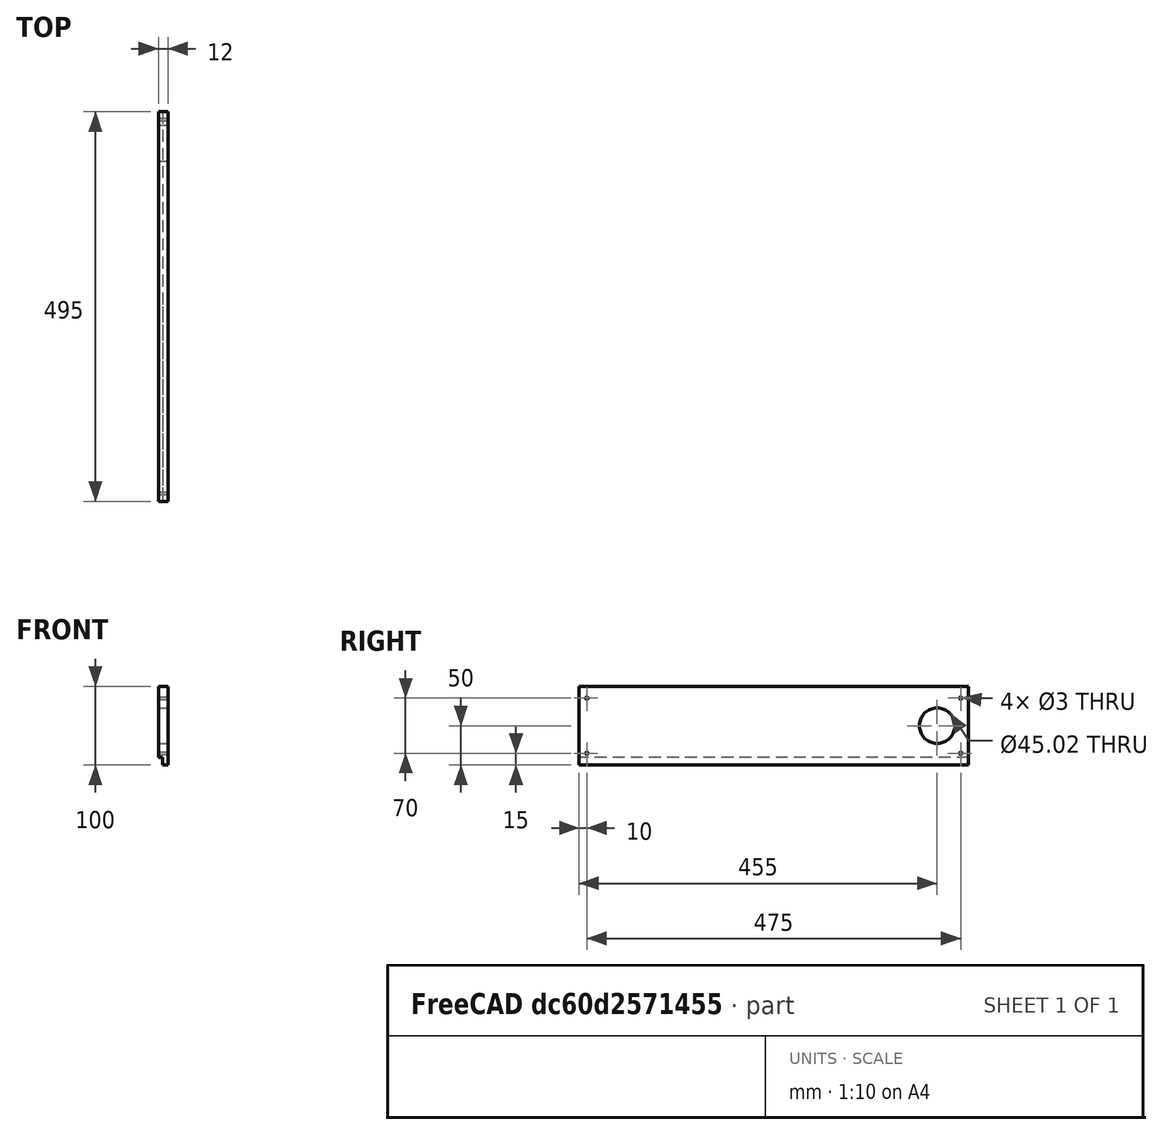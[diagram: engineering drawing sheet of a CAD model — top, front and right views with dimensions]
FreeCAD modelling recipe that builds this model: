
FCSTD DOCUMENT  (FreeCAD 0.20R29177 (Git))
Label: 8000_WindowFrameTopBack_
License: All rights reserved
LicenseURL: http://en.wikipedia.org/wiki/All_rights_reserved
objects: TechDraw::DrawViewDimension×8, Sketcher::SketchObject×3, PartDesign::Pocket×2, TechDraw::DrawViewPart×2, Spreadsheet::Sheet×1, PartDesign::Pad×1, TechDraw::DrawSVGTemplate×1, PartDesign::Body×1, TechDraw::DrawPage×1
note: 10 computed .brp shape members not serialized (recipe doc carries the construction recipe); baked Part::Feature solids carry a one-line shape summary decoded from their .brp

FEATURE [Sketcher::SketchObject] Sketch
  FullyConstrained = true
  MapMode = 4
  Placement = pos=(0,0,0) rot=(0.57735,0.57735,0.57735;2.0944rad)
  Support = -> [XY_Plane]
  expr: Constraints[5] = Spreadsheet.nZ
  expr: Constraints[6] = Spreadsheet.nY
  sketch-geometry (5):
    g0: LineSegment StartX=0 StartY=0 StartZ=0 EndX=0 EndY=100 EndZ=0
    g1: LineSegment StartX=495 StartY=0 StartZ=0 EndX=495 EndY=100 EndZ=0
    g2: LineSegment StartX=495 StartY=100 StartZ=0 EndX=0 EndY=100 EndZ=0
    g3: LineSegment StartX=247.5 StartY=0 StartZ=0 EndX=0 EndY=0 EndZ=0
    g4: LineSegment StartX=495 StartY=0 StartZ=0 EndX=247.5 EndY=0 EndZ=0
  constraints (14):
    c: Vertical(g0)
    c: Vertical(g1)
    c: Coincident(g2,g1)
    c: Coincident(g2,g0)
    c: Horizontal(g2)
    c: DistanceY(g1,g1) = 100
    c: DistanceX(g2,g2) = 495
    c: Coincident(g3,g0)
    c: Coincident(g4,g1)
    c: Horizontal(g4)
    c: Equal(g3,g4)
    c: Coincident(g4,g3)
    c: Horizontal(g3)
    c: Coincident(g0,g-1)
FEATURE [Spreadsheet::Sheet] Spreadsheet  label="xls"
  cells = B2=BODY FLOOR; E2=Ex.Ref.; B3=Thichness; C3=.T; D3=12; E3=mm; B7=KEYBOARD FRONT; D7=Sperrholz Birke 12 mm; B8=Width; C8=nY; D8(nY)=495; B9=Height; C9=nZ; D9(nZ)=100; E9=F(T); B10=Thickness; C10=nT; D10(nT)=12
FEATURE [PartDesign::Pad] Pad
  AllowMultiFace = false
  Direction = (1,1,1)
  Length = 12
  Length2 = 100
  Profile = -> Sketch
  Reversed = true
  Type = 0
  expr: Length = Spreadsheet.nT
FEATURE [Sketcher::SketchObject] Sketch001
  ExternalGeometry = -> [Pad]
  FullyConstrained = false
  MapMode = 5
  Placement = pos=(0,0,0) rot=(0.57735,0.57735,0.57735;2.0944rad)
  Support = -> [Pad]
  sketch-geometry (9):
    g0: LineSegment StartX=10 StartY=85 StartZ=0 EndX=485 EndY=85 EndZ=0
    g1: LineSegment StartX=485 StartY=85 StartZ=0 EndX=485 EndY=15 EndZ=0
    g2: LineSegment StartX=485 StartY=15 StartZ=0 EndX=10 EndY=15 EndZ=0
    g3: LineSegment StartX=10 StartY=15 StartZ=0 EndX=10 EndY=85 EndZ=0
    g4: Circle CenterX=10 CenterY=85 CenterZ=0 NormalX=0 NormalY=0 NormalZ=1 AngleXU=0 Radius=1.5
    g5: Circle CenterX=10 CenterY=15 CenterZ=0 NormalX=0 NormalY=0 NormalZ=1 AngleXU=0 Radius=1.5
    g6: Circle CenterX=485 CenterY=15 CenterZ=0 NormalX=0 NormalY=0 NormalZ=1 AngleXU=0 Radius=1.5
    g7: Circle CenterX=485 CenterY=85 CenterZ=0 NormalX=0 NormalY=0 NormalZ=1 AngleXU=0 Radius=1.5
    g8: Circle CenterX=455 CenterY=50 CenterZ=0 NormalX=0 NormalY=0 NormalZ=1 AngleXU=0 Radius=22.5086
  constraints (22):
    c: Coincident(g0,g1)
    c: Coincident(g1,g2)
    c: Coincident(g2,g3)
    c: Coincident(g3,g0)
    c: Horizontal(g0)
    c: Horizontal(g2)
    c: Vertical(g1)
    c: Vertical(g3)
    c: Coincident(g4,g0)
    c: Coincident(g5,g2)
    c: Coincident(g6,g1)
    c: Coincident(g7,g0)
    c: Equal(g4,g5)
    c: Equal(g5,g6)
    c: Equal(g6,g7)
    c: Diameter(g4) = 3
    c: DistanceY(g4,g-3) = 15
    c: DistanceX(g-3,g4) = 10
    c: DistanceY(g-1,g5) = 15
    c: DistanceX(g7,g-3) = 10
    c: DistanceX(g8,g-3) = 40
    c: DistanceY(g8,g-3) = 50
FEATURE [PartDesign::Pocket] Pocket
  BaseFeature = -> Pad
  Direction = (-1,0,0)
  Length = 5
  Length2 = 5
  Profile = -> Sketch001
  ReferenceAxis = -> Sketch001 [N_Axis]
  Type = 1
  UseCustomVector = true
FEATURE [TechDraw::DrawSVGTemplate] Template
  EditableTexts = Designed_by_Name=RIP 2023 09 17; Drawing_number=8000_WindowFrameTopBack; FC-Date=2024 06 20; FC-SC=0.4; FC-SH=1/1; FC-Title=Window Frame Back Pannel; Subtitle=Stabliizer Strut; Weight=?
  Height = 210
  Orientation = 1
  Width = 297
FEATURE [TechDraw::DrawViewPart] View
  CoarseView = false
  Direction = (1,0,0)
  Focus = 100
  HardHidden = false
  IsoCount = 0
  IsoHidden = false
  IsoVisible = false
  LockPosition = false
  Perspective = false
  Rotation = 0
  Scale = 0.4
  ScaleType = 2
  SeamHidden = false
  SeamVisible = true
  SmoothHidden = false
  SmoothVisible = true
  Source = -> [Pocket]
  X = 116.23
  XDirection = (0,1,0)
  Y = 132.805
FEATURE [TechDraw::DrawViewDimension] Dimension
  AngleOverride = false
  Arbitrary = false
  ArbitraryTolerances = false
  EqualTolerance = true
  ExtensionAngle = 0
  FormatSpec = %.2f
  FormatSpecOverTolerance = %+.2f
  FormatSpecUnderTolerance = %+.2f
  Inverted = false
  LineAngle = 0
  LockPosition = false
  MeasureType = 1
  OverTolerance = 0
  References2D = -> [View]
  Rotation = 0
  ScaleType = 0
  TheoreticalExact = false
  Type = 1
  UnderTolerance = 0
  X = 4.3299
  Y = 34.768
FEATURE [TechDraw::DrawViewDimension] Dimension001
  AngleOverride = false
  Arbitrary = false
  ArbitraryTolerances = false
  EqualTolerance = true
  ExtensionAngle = 0
  FormatSpec = %.2f
  FormatSpecOverTolerance = %+.2f
  FormatSpecUnderTolerance = %+.2f
  Inverted = false
  LineAngle = 0
  LockPosition = false
  MeasureType = 1
  OverTolerance = 0
  References2D = -> [View]
  Rotation = 0
  ScaleType = 0
  TheoreticalExact = false
  Type = 2
  UnderTolerance = 0
  X = -5.0026
  Y = 4.22818
FEATURE [TechDraw::DrawViewDimension] Dimension003
  AngleOverride = false
  Arbitrary = false
  ArbitraryTolerances = false
  EqualTolerance = true
  ExtensionAngle = 0
  FormatSpec = %.2f
  FormatSpecOverTolerance = %+.2f
  FormatSpecUnderTolerance = %+.2f
  Inverted = false
  LineAngle = 0
  LockPosition = false
  MeasureType = 1
  OverTolerance = 0
  References2D = -> [View]
  Rotation = 0
  ScaleType = 0
  TheoreticalExact = false
  Type = 2
  UnderTolerance = 0
  X = -84.3968
  Y = -1.49442
FEATURE [TechDraw::DrawViewDimension] Dimension004
  AngleOverride = false
  Arbitrary = false
  ArbitraryTolerances = false
  EqualTolerance = true
  ExtensionAngle = 0
  FormatSpec = ⌀%.2f
  FormatSpecOverTolerance = %+.2f
  FormatSpecUnderTolerance = %+.2f
  Inverted = false
  LineAngle = 0
  LockPosition = false
  MeasureType = 1
  OverTolerance = 0
  References2D = -> [View]
  Rotation = 0
  ScaleType = 0
  TheoreticalExact = false
  Type = 5
  UnderTolerance = 0
  X = 46.4435
  Y = 12.5167
FEATURE [Sketcher::SketchObject] Sketch002
  ExternalGeometry = -> [Pocket]
  FullyConstrained = true
  MapMode = 5
  Placement = pos=(0,495,0) rot=(0,0.707107,0.707107;3.14159rad)
  Support = -> [Pocket]
  sketch-geometry (4):
    g0: LineSegment StartX=12 StartY=0 StartZ=0 EndX=7 EndY=0 EndZ=0
    g1: LineSegment StartX=7 StartY=0 StartZ=0 EndX=7 EndY=10 EndZ=0
    g2: LineSegment StartX=7 StartY=10 StartZ=0 EndX=12 EndY=10 EndZ=0
    g3: LineSegment StartX=12 StartY=10 StartZ=0 EndX=12 EndY=0 EndZ=0
  constraints (11):
    c: Coincident(g0,g1)
    c: Coincident(g1,g2)
    c: Coincident(g2,g3)
    c: Coincident(g3,g0)
    c: Horizontal(g0)
    c: Horizontal(g2)
    c: Vertical(g1)
    c: Vertical(g3)
    c: Coincident(g0,g-4)
    c: DistanceY(g3,g3) = 10
    c: DistanceX(g2,g2) = 5
FEATURE [PartDesign::Pocket] Pocket001
  BaseFeature = -> Pocket
  Direction = (0,-1,2e-16)
  Length = 5
  Length2 = 5
  Profile = -> Sketch002
  ReferenceAxis = -> Sketch002 [N_Axis]
  Type = 1
FEATURE [PartDesign::Body] Body
  Group = -> [Sketch,Pad,Sketch001,Pocket,Sketch002,Pocket001]
  Origin = -> Origin
  Tip = -> Pocket001
FEATURE [TechDraw::DrawViewPart] View001
  CoarseView = false
  Direction = (0,1,0)
  Focus = 100
  HardHidden = false
  IsoCount = 0
  IsoHidden = false
  IsoVisible = false
  LockPosition = false
  Perspective = false
  Rotation = 0
  Scale = 0.5
  ScaleType = 2
  SeamHidden = false
  SeamVisible = true
  SmoothHidden = false
  SmoothVisible = true
  Source = -> [Pocket001]
  X = 238.198
  XDirection = (-1,0,0)
  Y = 128.518
FEATURE [TechDraw::DrawViewDimension] Dimension005
  AngleOverride = false
  Arbitrary = false
  ArbitraryTolerances = false
  EqualTolerance = true
  ExtensionAngle = 0
  FormatSpec = %.2f
  FormatSpecOverTolerance = %+.2f
  FormatSpecUnderTolerance = %+.2f
  Inverted = false
  LineAngle = 0
  LockPosition = false
  MeasureType = 1
  OverTolerance = 0
  References2D = -> [View001]
  Rotation = 0
  ScaleType = 0
  TheoreticalExact = false
  Type = 2
  UnderTolerance = 0
  X = 18.0764
  Y = -4.20318
FEATURE [TechDraw::DrawViewDimension] Dimension006
  AngleOverride = false
  Arbitrary = false
  ArbitraryTolerances = false
  EqualTolerance = true
  ExtensionAngle = 0
  FormatSpec = %.2f
  FormatSpecOverTolerance = %+.2f
  FormatSpecUnderTolerance = %+.2f
  Inverted = false
  LineAngle = 0
  LockPosition = false
  MeasureType = 1
  OverTolerance = 0
  References2D = -> [View001]
  Rotation = 0
  ScaleType = 0
  TheoreticalExact = false
  Type = 1
  UnderTolerance = 0
  X = -18.1672
  Y = -41.1956
FEATURE [TechDraw::DrawViewDimension] Dimension007
  AngleOverride = false
  Arbitrary = false
  ArbitraryTolerances = false
  EqualTolerance = true
  ExtensionAngle = 0
  FormatSpec = %.2f
  FormatSpecOverTolerance = %+.2f
  FormatSpecUnderTolerance = %+.2f
  Inverted = false
  LineAngle = 0
  LockPosition = false
  MeasureType = 1
  OverTolerance = 0
  References2D = -> [View001]
  Rotation = 0
  ScaleType = 0
  TheoreticalExact = false
  Type = 1
  UnderTolerance = 0
  X = 21.9423
  Y = 33.0614
FEATURE [TechDraw::DrawViewDimension] Dimension008
  AngleOverride = false
  Arbitrary = false
  ArbitraryTolerances = false
  EqualTolerance = true
  ExtensionAngle = 0
  FormatSpec = ⌀%.2f
  FormatSpecOverTolerance = %+.2f
  FormatSpecUnderTolerance = %+.2f
  Inverted = false
  LineAngle = 0
  LockPosition = false
  MeasureType = 1
  OverTolerance = 0
  References2D = -> [View]
  Rotation = 0
  ScaleType = 0
  TheoreticalExact = false
  Type = 5
  UnderTolerance = 0
  X = 55.7204
  Y = -29.6576
FEATURE [TechDraw::DrawPage] Page
  KeepUpdated = true
  NextBalloonIndex = 1
  ProjectionType = 0
  Template = -> Template
  Views = -> [View,Dimension,Dimension001,Dimension003,Dimension004,View001,Dimension005,Dimension006,Dimension007,Dimension008]
